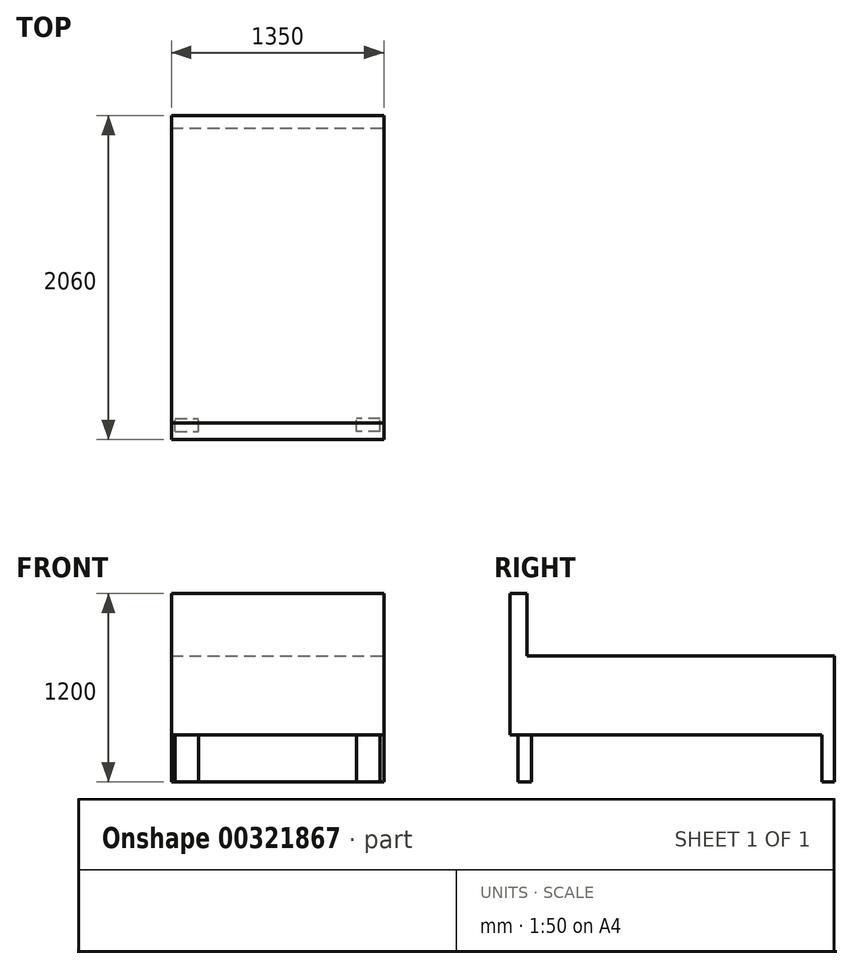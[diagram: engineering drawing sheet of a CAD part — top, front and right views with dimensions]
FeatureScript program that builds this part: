
annotation { "Feature Type Name" : "Feature", "Feature Type Description" : "" }
export const myFeature = defineFeature(function(context is Context, id is Id, definition is map)
    precondition{}
    {
        {
            var Q0;
            Q0=qCreatedBy(makeId("Top.planeOp"),FACE);
            var sketch = newSketch(context, id + "F0", { "sketchPlane" : qUnion([Q0])});
            skLineSegment(sketch, "E0.bottom", {"start": v(675, 1030) * mm, "end": v(-675, 1030) * mm});
            skLineSegment(sketch, "E0.top", {"start": v(675, -1030) * mm, "end": v(-675, -1030) * mm});
            skLineSegment(sketch, "E0.left", {"start": v(675, 1030) * mm, "end": v(675, -1030) * mm});
            skLineSegment(sketch, "E0.right", {"start": v(-675, 1030) * mm, "end": v(-675, -1030) * mm});
            skPoint(sketch, "E0.middle", {"position": v(0, 0) * mm});
            skSolve(sketch);
        }
        {
            var Q0;
            Q0 = qSketchRegion(id + "F0", true);
            var Q1;
            Q1=makeQuery(id+"F0.imprint","IMPRINT",FACE,{"disambiguationData":[TD([[makeQuery(id+"F0.imprint","IMPRINT",EDGE,{"derivedFrom":sQuery(id+"F0.wireOp",EDGE,"E0.bottom")}),1.0]])]});
            extrude(context, id + "F1", {"entities" : qUnion([Q0, Q1]), "depth" : 500 * mm});
        }
        {
            var Q0;
            Q0=makeQuery(id+"F1.opExtrude","CAP_FACE",FACE,{"disambiguationData":[OSD([sQuery(id+"F0.wireOp",EDGE,"E0.bottom"),sQuery(id+"F0.wireOp",EDGE,"E0.top"),sQuery(id+"F0.wireOp",EDGE,"E0.left"),sQuery(id+"F0.wireOp",EDGE,"E0.right")])],"isStart":true});
            var sketch = newSketch(context, id + "F2", { "sketchPlane" : qUnion([Q0])});
            skLineSegment(sketch, "E1", {"start": v(0, -1030) * mm, "end": v(0, 1030) * mm, "construction": true});
            skLineSegment(sketch, "E2", {"start": v(-675, 0) * mm, "end": v(675, 0) * mm, "construction": true});
            skLineSegment(sketch, "E3.bottom", {"start": v(-675, -1030) * mm, "end": v(675, -1030) * mm});
            skLineSegment(sketch, "E3.top", {"start": v(-675, -950.8) * mm, "end": v(675, -950.8) * mm});
            skLineSegment(sketch, "E3.left", {"start": v(-675, -1030) * mm, "end": v(-675, -950.8) * mm});
            skLineSegment(sketch, "E3.right", {"start": v(675, -1030) * mm, "end": v(675, -950.8) * mm});
            skLineSegment(sketch, "E4.bottom", {"start": v(-650.95, 978.99) * mm, "end": v(-502.3, 978.99) * mm});
            skLineSegment(sketch, "E4.top", {"start": v(-650.95, 894.42) * mm, "end": v(-502.3, 894.42) * mm});
            skLineSegment(sketch, "E4.left", {"start": v(-502.3, 978.99) * mm, "end": v(-502.3, 894.42) * mm});
            skLineSegment(sketch, "E4.right", {"start": v(-650.95, 978.99) * mm, "end": v(-650.95, 894.42) * mm});
            skLineSegment(sketch, "E5.MirrorCS", {"start": v(502.3, 978.99) * mm, "end": v(502.3, 894.42) * mm});
            skLineSegment(sketch, "E6.MirrorCS", {"start": v(650.95, 894.42) * mm, "end": v(502.3, 894.42) * mm});
            skLineSegment(sketch, "E7.MirrorCS", {"start": v(650.95, 978.99) * mm, "end": v(502.3, 978.99) * mm});
            skLineSegment(sketch, "E8.MirrorCS", {"start": v(650.95, 978.99) * mm, "end": v(650.95, 894.42) * mm});
            skSolve(sketch);
        }
        {
            var Q0;
            Q0 = qSketchRegion(id + "F2", true);
            extrude(context, id + "F3", {"entities" : qUnion([Q0]), "operationType" : NewBodyOperationType.ADD, "depth" : 300 * mm});
        }
        {
            var Q0;
            Q0=makeQuery(id+"F1.opExtrude","CAP_FACE",FACE,{"disambiguationData":[OSD([sQuery(id+"F0.wireOp",EDGE,"E0.bottom"),sQuery(id+"F0.wireOp",EDGE,"E0.top"),sQuery(id+"F0.wireOp",EDGE,"E0.left"),sQuery(id+"F0.wireOp",EDGE,"E0.right")])],"isStart":false});
            var sketch = newSketch(context, id + "F4", { "sketchPlane" : qUnion([Q0])});
            skLineSegment(sketch, "E9.bottom", {"start": v(-675, -1030) * mm, "end": v(675, -1030) * mm});
            skLineSegment(sketch, "E9.top", {"start": v(-675, -922.9) * mm, "end": v(675, -922.9) * mm});
            skLineSegment(sketch, "E9.left", {"start": v(-675, -1030) * mm, "end": v(-675, -922.9) * mm});
            skLineSegment(sketch, "E9.right", {"start": v(675, -1030) * mm, "end": v(675, -922.9) * mm});
            skSolve(sketch);
        }
        {
            var Q0;
            Q0 = qSketchRegion(id + "F4", true);
            extrude(context, id + "F5", {"entities" : qUnion([Q0]), "operationType" : NewBodyOperationType.ADD, "depth" : 400 * mm});
        }
    });
